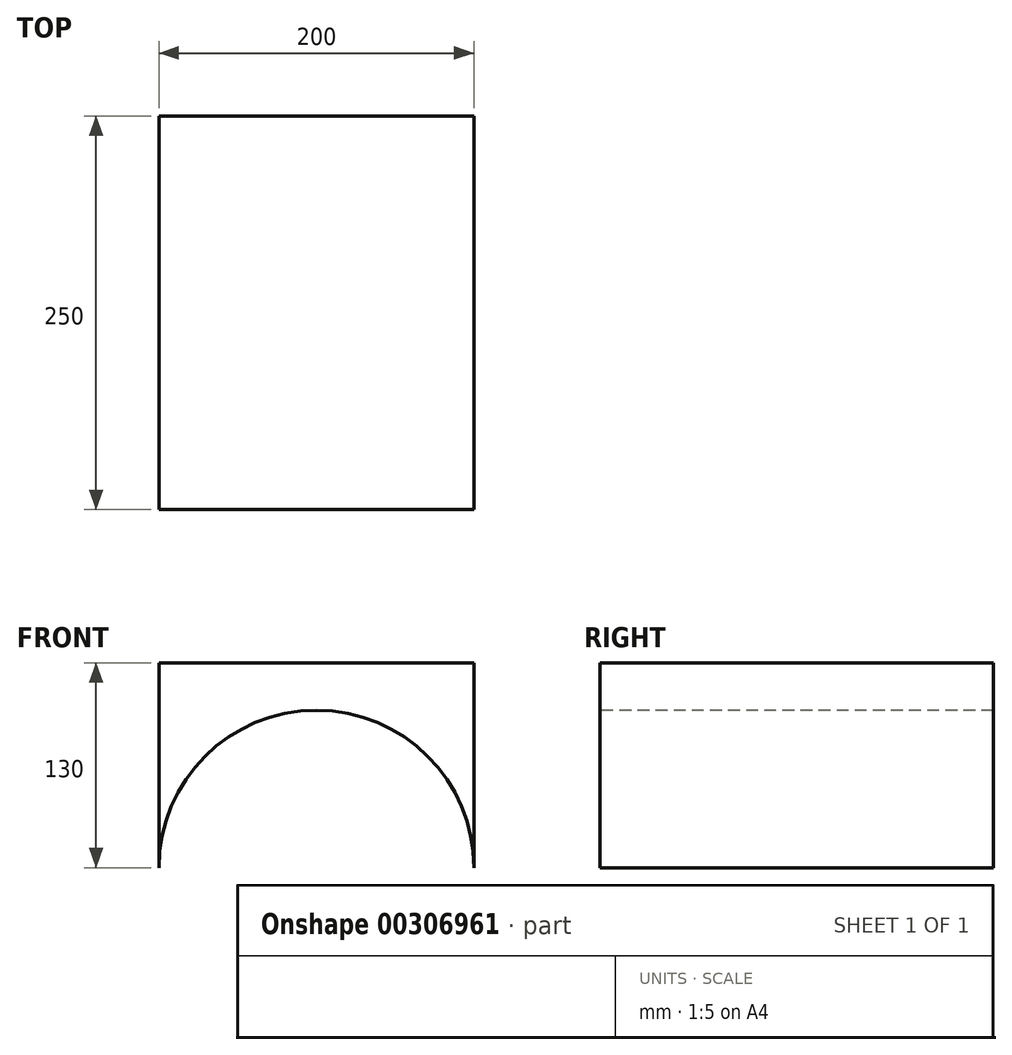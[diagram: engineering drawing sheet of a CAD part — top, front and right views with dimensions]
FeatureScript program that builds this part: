
annotation { "Feature Type Name" : "Feature", "Feature Type Description" : "" }
export const myFeature = defineFeature(function(context is Context, id is Id, definition is map)
    precondition{}
    {
        {
            var Q0;
            Q0=qCreatedBy(makeId("Front.planeOp"),FACE);
            var sketch = newSketch(context, id + "F0", { "sketchPlane" : qUnion([Q0])});
            skArc(sketch, "E0", {"start": v(100, 0) * mm, "mid": v(0, 100) * mm, "end": v(-100, 0) * mm});
            skLineSegment(sketch, "E1", {"start": v(-100, 0) * mm, "end": v(-100, 130) * mm});
            skLineSegment(sketch, "E2", {"start": v(-100, 130) * mm, "end": v(100, 130) * mm});
            skLineSegment(sketch, "E3", {"start": v(100, 130) * mm, "end": v(100, 0) * mm});
            skSolve(sketch);
        }
        {
            var Q0;
            Q0 = qSketchRegion(id + "F0", true);
            extrude(context, id + "F1", {"entities" : qUnion([Q0]), "oppositeDirection" : true, "depth" : 250 * mm});
        }
    });
